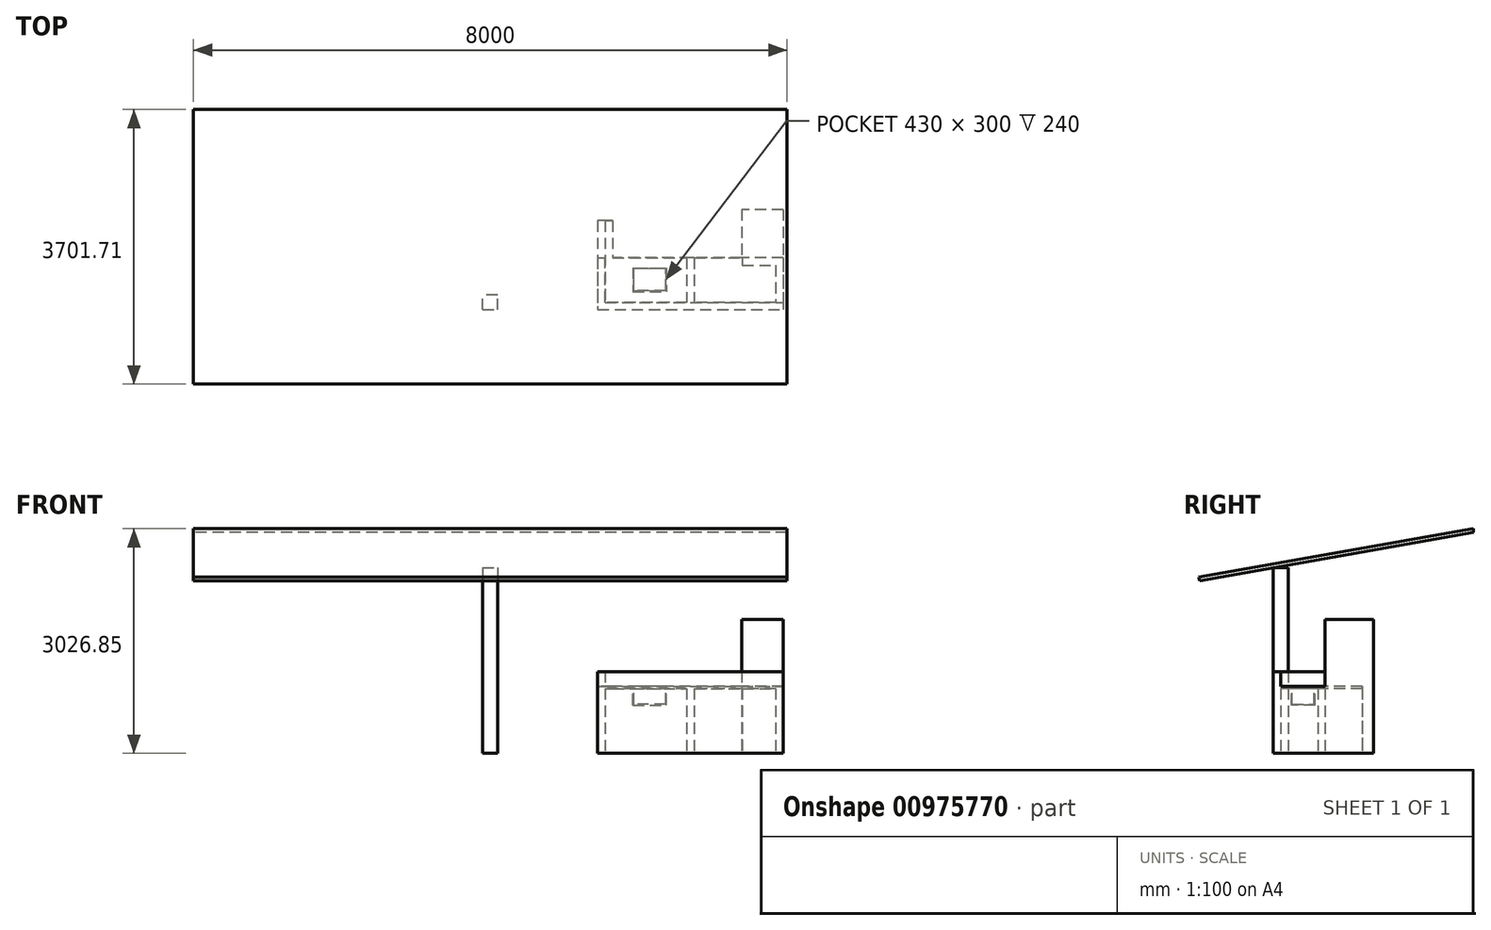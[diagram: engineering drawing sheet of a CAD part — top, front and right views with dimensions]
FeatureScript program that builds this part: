
annotation { "Feature Type Name" : "Feature", "Feature Type Description" : "" }
export const myFeature = defineFeature(function(context is Context, id is Id, definition is map)
    precondition{}
    {
        {
            var Q0;
            Q0=qCreatedBy(makeId("Top.planeOp"),FACE);
            var sketch = newSketch(context, id + "F0", { "sketchPlane" : qUnion([Q0])});
            skLineSegment(sketch, "E0.bottom", {"start": v(-3950, 10000) * mm, "end": v(3950, 10000) * mm});
            skLineSegment(sketch, "E0.top", {"start": v(-3950, -10000) * mm, "end": v(3950, -10000) * mm});
            skLineSegment(sketch, "E0.left", {"start": v(-3950, 10000) * mm, "end": v(-3950, -10000) * mm});
            skLineSegment(sketch, "E0.right", {"start": v(3950, 10000) * mm, "end": v(3950, -10000) * mm});
            skPoint(sketch, "E1", {"position": v(0, 10000) * mm});
            skPoint(sketch, "E2", {"position": v(3950, 0) * mm});
            skLineSegment(sketch, "E3", {"start": v(-3950, 7300) * mm, "end": v(3950, 7300) * mm});
            skLineSegment(sketch, "E4", {"start": v(3400, 10000) * mm, "end": v(3400, 8000) * mm});
            skLineSegment(sketch, "E5", {"start": v(3400, 8000) * mm, "end": v(1650, 8000) * mm});
            skLineSegment(sketch, "E6", {"start": v(1650, 8000) * mm, "end": v(1650, 8500) * mm});
            skLineSegment(sketch, "E7", {"start": v(1650, 8500) * mm, "end": v(1450, 8500) * mm});
            skLineSegment(sketch, "E8", {"start": v(1450, 8500) * mm, "end": v(1450, 7300) * mm});
            skLineSegment(sketch, "E9", {"start": v(3950, 5800) * mm, "end": v(2280, 5800) * mm});
            skLineSegment(sketch, "E10", {"start": v(2280, 5800) * mm, "end": v(2280, 2800) * mm});
            skLineSegment(sketch, "E11", {"start": v(2280, 2800) * mm, "end": v(-3950, 2800) * mm});
            skLineSegment(sketch, "E12", {"start": v(-2410, 2800) * mm, "end": v(-2410, -2599) * mm});
            skLineSegment(sketch, "E13", {"start": v(-2410, -2599) * mm, "end": v(-3950, -2599) * mm});
            skLineSegment(sketch, "E14.bottom", {"start": v(2380, 5700) * mm, "end": v(3850, 5700) * mm});
            skLineSegment(sketch, "E14.top", {"start": v(2380, 2800) * mm, "end": v(3850, 2800) * mm});
            skLineSegment(sketch, "E14.left", {"start": v(2380, 5700) * mm, "end": v(2380, 2800) * mm});
            skLineSegment(sketch, "E14.right", {"start": v(3850, 5700) * mm, "end": v(3850, 2800) * mm});
            skLineSegment(sketch, "E15.bottom", {"start": v(950, 2700) * mm, "end": v(3850, 2700) * mm});
            skLineSegment(sketch, "E15.top", {"start": v(950, -750) * mm, "end": v(3850, -750) * mm});
            skLineSegment(sketch, "E15.left", {"start": v(950, 2700) * mm, "end": v(950, -750) * mm});
            skLineSegment(sketch, "E15.right", {"start": v(3850, 2700) * mm, "end": v(3850, -750) * mm});
            skLineSegment(sketch, "E16.bottom", {"start": v(850, 2700) * mm, "end": v(-2310, 2700) * mm});
            skLineSegment(sketch, "E16.left", {"start": v(850, 2700) * mm, "end": v(850, 270) * mm});
            skLineSegment(sketch, "E16.right", {"start": v(-2310, 2700) * mm, "end": v(-2310, -750) * mm});
            skLineSegment(sketch, "E17.bottom", {"start": v(-170, 270) * mm, "end": v(850, 270) * mm});
            skLineSegment(sketch, "E17.left", {"start": v(-170, 270) * mm, "end": v(-170, -750) * mm});
            skLineSegment(sketch, "E18.trimOffspring", {"start": v(-170, -750) * mm, "end": v(-2310, -750) * mm});
            skSolve(sketch);
        }
        {
            var Q0;
            {var subQ0=sQuery(id+"F0.wireOp",EDGE,"E4");Q0=makeQuery(id+"F0.imprint","IMPRINT",FACE,{"disambiguationData":[TD([[makeQuery(id+"F0.imprint","IMPRINT",EDGE,{"derivedFrom":subQ0}),1.0]])]});}
            var Q1;
            {var subQ0=sQuery(id+"F0.wireOp",EDGE,"E4");Q1=makeQuery(id+"F0.imprint","IMPRINT",FACE,{"disambiguationData":[TD([[makeQuery(id+"F0.imprint","IMPRINT",EDGE,{"derivedFrom":subQ0}),1.0]])]});}
            var sketch = newSketch(context, id + "F1", { "sketchPlane" : qUnion([Q0, Q1])});
            skLineSegment(sketch, "E19.bottom", {"start": v(1550, 7400) * mm, "end": v(2650, 7400) * mm});
            skLineSegment(sketch, "E20.bottom", {"start": v(1450, 8500) * mm, "end": v(1550, 8500) * mm});
            skLineSegment(sketch, "E20.right", {"start": v(1550, 8500) * mm, "end": v(1550, 7400) * mm});
            skLineSegment(sketch, "E21.bottom", {"start": v(2650, 8000) * mm, "end": v(2750, 8000) * mm});
            skLineSegment(sketch, "E21.left", {"start": v(2650, 8000) * mm, "end": v(2650, 7400) * mm});
            skLineSegment(sketch, "E21.right", {"start": v(2750, 8000) * mm, "end": v(2750, 7400) * mm});
            skLineSegment(sketch, "E22.trimOffspring", {"start": v(2750, 7400) * mm, "end": v(3850, 7400) * mm});
            skLineSegment(sketch, "E23.left", {"start": v(3850, 7900) * mm, "end": v(3850, 7400) * mm});
            skLineSegment(sketch, "E24.bottom", {"start": v(3400, 8000) * mm, "end": v(3950, 8000) * mm});
            skLineSegment(sketch, "E24.left", {"start": v(3400, 8000) * mm, "end": v(3400, 7900) * mm});
            skLineSegment(sketch, "E25", {"start": v(1450, 8500) * mm, "end": v(1450, 7300) * mm});
            skLineSegment(sketch, "E26", {"start": v(1450, 7300) * mm, "end": v(3950, 7300) * mm});
            skLineSegment(sketch, "E27", {"start": v(3950, 7300) * mm, "end": v(3950, 8000) * mm});
            skLineSegment(sketch, "E28", {"start": v(3400, 7900) * mm, "end": v(3850, 7900) * mm});
            skSolve(sketch);
        }
        {
            var Q0;
            Q0 = qSketchRegion(id + "F1", true);
            extrude(context, id + "F2", {"entities" : qUnion([Q0]), "depth" : 1100 * mm, "offsetDistance" : 25 * mm});
        }
        {
            var Q0;
            Q0=makeQuery(id+"F2.opExtrude","CAP_FACE",FACE,{"disambiguationData":[OSD([sQuery(id+"F1.wireOp",EDGE,"E19.bottom"),sQuery(id+"F1.wireOp",EDGE,"E19.top"),sQuery(id+"F1.wireOp",EDGE,"E19.right"),sQuery(id+"F1.wireOp",EDGE,"E20.bottom"),sQuery(id+"F1.wireOp",EDGE,"E20.left"),sQuery(id+"F1.wireOp",EDGE,"E20.right"),sQuery(id+"F1.wireOp",EDGE,"E21.bottom"),sQuery(id+"F1.wireOp",EDGE,"E21.left"),sQuery(id+"F1.wireOp",EDGE,"E21.right"),sQuery(id+"F1.wireOp",EDGE,"E22.trimOffspring")])],"isStart":false});
            var sketch = newSketch(context, id + "F3", { "sketchPlane" : qUnion([Q0])});
            skPoint(sketch, "E29.oppositeSnap0", {"position": v(1450, 8000) * mm});
            skLineSegment(sketch, "E29.bottom", {"start": v(1450, 8500) * mm, "end": v(1550, 8500) * mm});
            skLineSegment(sketch, "E29.top", {"start": v(1450, 8000) * mm, "end": v(1550, 8000) * mm});
            skLineSegment(sketch, "E29.left", {"start": v(1450, 8500) * mm, "end": v(1450, 8000) * mm});
            skLineSegment(sketch, "E29.right", {"start": v(1550, 8500) * mm, "end": v(1550, 8000) * mm});
            skLineSegment(sketch, "E30.bottom", {"start": v(2650, 8000) * mm, "end": v(2750, 8000) * mm});
            skLineSegment(sketch, "E30.top", {"start": v(2650, 7400) * mm, "end": v(2750, 7400) * mm});
            skLineSegment(sketch, "E30.left", {"start": v(2650, 8000) * mm, "end": v(2650, 7400) * mm});
            skLineSegment(sketch, "E30.right", {"start": v(2750, 8000) * mm, "end": v(2750, 7400) * mm});
            skLineSegment(sketch, "E31", {"start": v(3400, 8000) * mm, "end": v(3950, 8000) * mm});
            skLineSegment(sketch, "E32", {"start": v(3950, 8000) * mm, "end": v(3950, 7400) * mm});
            skLineSegment(sketch, "E33", {"start": v(3950, 7400) * mm, "end": v(3400, 7400) * mm});
            skLineSegment(sketch, "E34", {"start": v(3850, 7400) * mm, "end": v(3850, 7400) * mm});
            skLineSegment(sketch, "E35", {"start": v(3400, 8000) * mm, "end": v(3400, 8000) * mm});
            skLineSegment(sketch, "E36", {"start": v(3400, 8000) * mm, "end": v(3400, 7400) * mm});
            skSolve(sketch);
        }
        {
            var Q0;
            Q0 = qSketchRegion(id + "F3", true);
            extrude(context, id + "F4", {"entities" : qUnion([Q0]), "operationType" : NewBodyOperationType.REMOVE, "oppositeDirection" : true, "depth" : 200 * mm, "offsetDistance" : 25 * mm});
        }
        {
            var Q0;
            Q0=makeQuery(id+"F4.boolean.opBoolean","COPY",FACE,{"derivedFrom":makeQuery(id+"F4.opExtrude","CAP_FACE",FACE,{"disambiguationData":[OSD([sQuery(id+"F3.wireOp",EDGE,"E30.bottom"),sQuery(id+"F3.wireOp",EDGE,"E30.top"),sQuery(id+"F3.wireOp",EDGE,"E30.left"),sQuery(id+"F3.wireOp",EDGE,"E30.right")])],"isStart":false})});
            var sketch = newSketch(context, id + "F5", { "sketchPlane" : qUnion([Q0])});
            skLineSegment(sketch, "E37", {"start": v(1650, 8500) * mm, "end": v(1650, 8000) * mm});
            skLineSegment(sketch, "E38", {"start": v(1650, 8000) * mm, "end": v(3400, 8000) * mm});
            skLineSegment(sketch, "E39", {"start": v(3400, 8000) * mm, "end": v(3950, 8000) * mm});
            skLineSegment(sketch, "E40", {"start": v(3950, 8000) * mm, "end": v(3950, 7400) * mm});
            skLineSegment(sketch, "E41", {"start": v(3950, 7400) * mm, "end": v(1550, 7400) * mm});
            skLineSegment(sketch, "E42", {"start": v(1550, 7400) * mm, "end": v(1550, 8000) * mm});
            skLineSegment(sketch, "E43", {"start": v(1550, 8000) * mm, "end": v(1450, 8000) * mm});
            skLineSegment(sketch, "E44", {"start": v(1450, 8000) * mm, "end": v(1450, 8500) * mm});
            skLineSegment(sketch, "E45", {"start": v(1450, 8500) * mm, "end": v(1650, 8500) * mm});
            skLineSegment(sketch, "E46", {"start": v(3400, 8000) * mm, "end": v(3400, 8000) * mm});
            skSolve(sketch);
        }
        {
            var Q0;
            Q0 = qSketchRegion(id + "F5", true);
            extrude(context, id + "F6", {"entities" : qUnion([Q0]), "operationType" : NewBodyOperationType.ADD, "oppositeDirection" : true, "depth" : 30 * mm, "offsetDistance" : 25 * mm});
        }
        {
            var Q0;
            Q0=makeQuery(id+"F6.boolean.opBoolean","MERGE",FACE,{"derivedFrom":[makeQuery(id+"F4.boolean.opBoolean","COPY",FACE,{"derivedFrom":makeQuery(id+"F4.opExtrude","CAP_FACE",FACE,{"disambiguationData":[OSD([sQuery(id+"F3.wireOp",EDGE,"E29.bottom"),sQuery(id+"F3.wireOp",EDGE,"E29.top"),sQuery(id+"F3.wireOp",EDGE,"E29.left"),sQuery(id+"F3.wireOp",EDGE,"E29.right")])],"isStart":false})}),makeQuery(id+"F4.boolean.opBoolean","COPY",FACE,{"derivedFrom":makeQuery(id+"F4.opExtrude","CAP_FACE",FACE,{"disambiguationData":[OSD([sQuery(id+"F3.wireOp",EDGE,"E30.bottom"),sQuery(id+"F3.wireOp",EDGE,"E30.top"),sQuery(id+"F3.wireOp",EDGE,"E30.left"),sQuery(id+"F3.wireOp",EDGE,"E30.right")])],"isStart":false})}),makeQuery(id+"F6.opExtrude","CAP_FACE",FACE,{"disambiguationData":[OSD([sQuery(id+"F5.wireOp",EDGE,"E37"),sQuery(id+"F5.wireOp",EDGE,"E38"),sQuery(id+"F5.wireOp",EDGE,"2jL8oUfe-vOBU-r91h-opIe-e30LOmFQffgg"),sQuery(id+"F5.wireOp",EDGE,"E39"),sQuery(id+"F5.wireOp",EDGE,"E40"),sQuery(id+"F5.wireOp",EDGE,"E41"),sQuery(id+"F5.wireOp",EDGE,"E42"),sQuery(id+"F5.wireOp",EDGE,"E43"),sQuery(id+"F5.wireOp",EDGE,"E44"),sQuery(id+"F5.wireOp",EDGE,"E45")])],"isStart":true})]});
            var sketch = newSketch(context, id + "F7", { "sketchPlane" : qUnion([Q0])});
            skLineSegment(sketch, "E47.bottom", {"start": v(1925, 7864.36) * mm, "end": v(2375, 7864.36) * mm});
            skLineSegment(sketch, "E47.top", {"start": v(1925, 7544.36) * mm, "end": v(2375, 7544.36) * mm});
            skLineSegment(sketch, "E47.left", {"start": v(1925, 7864.36) * mm, "end": v(1925, 7544.36) * mm});
            skLineSegment(sketch, "E47.right", {"start": v(2375, 7864.36) * mm, "end": v(2375, 7544.36) * mm});
            skLineSegment(sketch, "E48", {"start": v(2750, 8000) * mm, "end": v(2750, 7400) * mm, "construction": true});
            skPoint(sketch, "E49", {"position": v(2150, 7864.36) * mm});
            skSolve(sketch);
        }
        {
            var Q0;
            Q0=makeQuery(id+"F7.imprint","IMPRINT",FACE,{"disambiguationData":[TD([[makeQuery(id+"F7.imprint","IMPRINT",EDGE,{"derivedFrom":sQuery(id+"F7.wireOp",EDGE,"E47.bottom")}),-1.0]])]});
            extrude(context, id + "F8", {"entities" : qUnion([Q0]), "operationType" : NewBodyOperationType.ADD, "oppositeDirection" : true, "depth" : 250 * mm, "offsetDistance" : 25 * mm});
        }
        {
            var Q0;
            Q0=makeQuery(id+"F7.imprint","IMPRINT",FACE,{"disambiguationData":[TD([[makeQuery(id+"F7.imprint","IMPRINT",EDGE,{"derivedFrom":sQuery(id+"F7.wireOp",EDGE,"E47.bottom")}),-1.0]])]});
            var sketch = newSketch(context, id + "F9", { "sketchPlane" : qUnion([Q0])});
            skLineSegment(sketch, "E50.bottom", {"start": v(2365, 7554.36) * mm, "end": v(1935, 7554.36) * mm});
            skLineSegment(sketch, "E50.top", {"start": v(2365, 7854.36) * mm, "end": v(1935, 7854.36) * mm});
            skLineSegment(sketch, "E50.left", {"start": v(2365, 7554.36) * mm, "end": v(2365, 7854.36) * mm});
            skLineSegment(sketch, "E50.right", {"start": v(1935, 7554.36) * mm, "end": v(1935, 7854.36) * mm});
            skSolve(sketch);
        }
        {
            var Q0;
            Q0=makeQuery(id+"F9.imprint","IMPRINT",FACE,{"disambiguationData":[TD([[makeQuery(id+"F9.imprint","IMPRINT",EDGE,{"derivedFrom":sQuery(id+"F9.wireOp",EDGE,"E50.bottom")}),-1.0]])]});
            extrude(context, id + "F10", {"entities" : qUnion([Q0]), "operationType" : NewBodyOperationType.REMOVE, "oppositeDirection" : true, "depth" : 240 * mm, "offsetDistance" : 25 * mm});
        }
        {
            var Q0;
            {var subQ0=sQuery(id+"F0.wireOp",EDGE,"E4");Q0=makeQuery(id+"F0.imprint","IMPRINT",FACE,{"disambiguationData":[TD([[makeQuery(id+"F0.imprint","IMPRINT",EDGE,{"derivedFrom":subQ0}),1.0]])]});}
            var sketch = newSketch(context, id + "F11", { "sketchPlane" : qUnion([Q0])});
            skLineSegment(sketch, "E51.bottom", {"start": v(3950, 8650) * mm, "end": v(3390, 8650) * mm});
            skLineSegment(sketch, "E51.top", {"start": v(3950, 8000) * mm, "end": v(3390, 8000) * mm});
            skLineSegment(sketch, "E51.left", {"start": v(3950, 8650) * mm, "end": v(3950, 8000) * mm});
            skLineSegment(sketch, "E51.right", {"start": v(3390, 8650) * mm, "end": v(3390, 8000) * mm});
            skSolve(sketch);
        }
        {
            var Q0;
            Q0 = qSketchRegion(id + "F11", true);
            extrude(context, id + "F12", {"entities" : qUnion([Q0]), "operationType" : NewBodyOperationType.ADD, "depth" : 1800 * mm, "offsetDistance" : 25 * mm});
        }
        {
            var Q0;
            {var subQ0=sQuery(id+"F0.wireOp",EDGE,"E4");Q0=makeQuery(id+"F0.imprint","IMPRINT",FACE,{"disambiguationData":[TD([[makeQuery(id+"F0.imprint","IMPRINT",EDGE,{"derivedFrom":subQ0}),-1.0]])]});}
            var Q1;
            {var subQ0=sQuery(id+"F0.wireOp",EDGE,"E4");Q1=makeQuery(id+"F0.imprint","IMPRINT",FACE,{"disambiguationData":[TD([[makeQuery(id+"F0.imprint","IMPRINT",EDGE,{"derivedFrom":subQ0}),-1.0]])]});}
            var Q2;
            Q2=qCreatedBy(makeId("Top.planeOp"),FACE);
            var Q3;
            {var subQ0=sQuery(id+"F0.wireOp",EDGE,"E4");Q3=makeQuery(id+"F0.imprint","IMPRINT",FACE,{"disambiguationData":[TD([[makeQuery(id+"F0.imprint","IMPRINT",EDGE,{"derivedFrom":subQ0}),-1.0]])]});}
            var sketch = newSketch(context, id + "F13", { "sketchPlane" : qUnion([Q0, Q1, Q2, Q3])});
            skLineSegment(sketch, "E52.bottom", {"start": v(100, 7300) * mm, "end": v(-100, 7300) * mm});
            skLineSegment(sketch, "E52.top", {"start": v(100, 7500) * mm, "end": v(-100, 7500) * mm});
            skLineSegment(sketch, "E52.left", {"start": v(100, 7300) * mm, "end": v(100, 7500) * mm});
            skLineSegment(sketch, "E52.right", {"start": v(-100, 7300) * mm, "end": v(-100, 7500) * mm});
            skPoint(sketch, "E53", {"position": v(0, 7300) * mm});
            skSolve(sketch);
        }
        {
            var Q0;
            Q0 = qSketchRegion(id + "F13", true);
            extrude(context, id + "F14", {"entities" : qUnion([Q0]), "depth" : 2500 * mm, "offsetDistance" : 25 * mm});
        }
        {
            var Q0;
            Q0=qCreatedBy(makeId("Right.planeOp"),FACE);
            var sketch = newSketch(context, id + "F15", { "sketchPlane" : qUnion([Q0])});
            skLineSegment(sketch, "E54.bottom", {"start": v(7300, 2500) * mm, "end": v(10000, 2976.08) * mm, "construction": true});
            skLineSegment(sketch, "E54.top", {"start": v(7300, 0) * mm, "end": v(10000, 0) * mm, "construction": true});
            skLineSegment(sketch, "E54.left", {"start": v(7300, 2500) * mm, "end": v(7300, 0) * mm, "construction": true});
            skLineSegment(sketch, "E54.right", {"start": v(10000, 2976.08) * mm, "end": v(10000, 0) * mm, "construction": true});
            skLineSegment(sketch, "E55", {"start": v(10000, 2976.08) * mm, "end": v(6306.97, 2324.9) * mm});
            skLineSegment(sketch, "E56", {"start": v(6306.97, 2324.9) * mm, "end": v(6298.29, 2374.14) * mm});
            skLineSegment(sketch, "E57", {"start": v(6298.29, 2374.14) * mm, "end": v(10000, 3026.85) * mm});
            skLineSegment(sketch, "E58", {"start": v(10000, 3026.85) * mm, "end": v(10000, 2976.08) * mm});
            skSolve(sketch);
        }
        {
            var Q0;
            Q0 = qSketchRegion(id + "F15", true);
            extrude(context, id + "F16", {"entities" : qUnion([Q0]), "depth" : 4000 * mm, "offsetDistance" : 25 * mm, "hasSecondDirection" : true, "secondDirectionOppositeDirection" : true, "secondDirectionDepth" : 4000 * mm});
        }
    });
